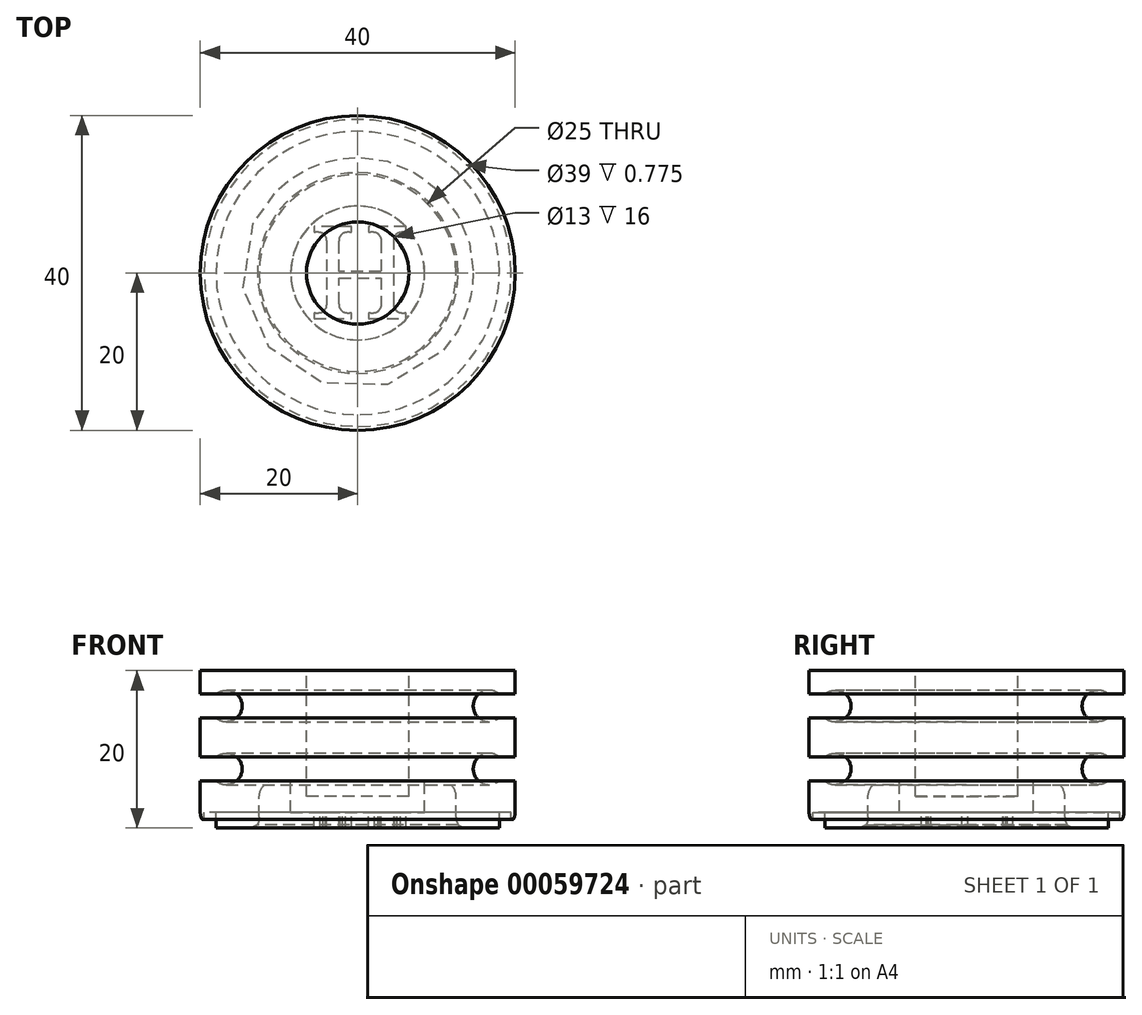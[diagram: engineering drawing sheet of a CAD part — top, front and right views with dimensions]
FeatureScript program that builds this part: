
annotation { "Feature Type Name" : "Feature", "Feature Type Description" : "" }
export const myFeature = defineFeature(function(context is Context, id is Id, definition is map)
    precondition{}
    {
        {
            var Q0;
            Q0=qCreatedBy(makeId("Top.planeOp"),FACE);
            var sketch = newSketch(context, id + "F0", { "sketchPlane" : qUnion([Q0])});
            skCircle(sketch, "E0", {"center": v(0, 0) * mm, "radius": 20 * mm});
            skSolve(sketch);
        }
        {
            var Q0;
            Q0=makeQuery(id+"F0.imprint","IMPRINT",FACE,{"disambiguationData":[TD([[makeQuery(id+"F0.imprint","IMPRINT",EDGE,{"derivedFrom":sQuery(id+"F0.wireOp",EDGE,"E0")}),1.0]])]});
            extrude(context, id + "F1", {"entities" : qUnion([Q0]), "depth" : 20 * mm});
        }
        {
            var Q0;
            Q0=qCreatedBy(makeId("Front.planeOp"),FACE);
            var sketch = newSketch(context, id + "F2", { "sketchPlane" : qUnion([Q0])});
            skLineSegment(sketch, "E1", {"start": v(-6.5, 20) * mm, "end": v(-20, 20) * mm});
            skLineSegment(sketch, "E2", {"start": v(-20, 20) * mm, "end": v(-20, 17) * mm});
            skLineSegment(sketch, "E3", {"start": v(-18, 0) * mm, "end": v(-13.97, 0) * mm});
            skLineSegment(sketch, "E4.bottom", {"start": v(-20, 17) * mm, "end": v(-18, 17) * mm});
            skLineSegment(sketch, "E4.top", {"start": v(-20, 14) * mm, "end": v(-18, 14) * mm});
            skLineSegment(sketch, "E5.bottom", {"start": v(-20, 9) * mm, "end": v(-18, 9) * mm});
            skLineSegment(sketch, "E5.top", {"start": v(-20, 6) * mm, "end": v(-18, 6) * mm});
            skArc(sketch, "E6", {"start": v(-18, 14) * mm, "mid": v(-14.68, 15.5) * mm, "end": v(-18, 17) * mm});
            skPoint(sketch, "E6.centerSnap0", {"position": v(-18, 15.5) * mm});
            skArc(sketch, "E7", {"start": v(-18, 6) * mm, "mid": v(-14.68, 7.5) * mm, "end": v(-18, 9) * mm});
            skPoint(sketch, "E7.centerSnap0", {"position": v(-18, 7.5) * mm});
            skLineSegment(sketch, "E8.trimOffspring", {"start": v(-20, 6) * mm, "end": v(-20, 2) * mm});
            skLineSegment(sketch, "E9.trimOffspring", {"start": v(-20, 14) * mm, "end": v(-20, 9) * mm});
            skLineSegment(sketch, "E10", {"start": v(0, 20) * mm, "end": v(0, 23.33) * mm});
            skLineSegment(sketch, "E11", {"start": v(0, 23.33) * mm, "end": v(-23.04, 23.33) * mm});
            skLineSegment(sketch, "E12", {"start": v(-23.04, 23.33) * mm, "end": v(-23.04, -1.84) * mm});
            skLineSegment(sketch, "E13", {"start": v(-23.04, -1.84) * mm, "end": v(0, -1.84) * mm});
            skLineSegment(sketch, "E14", {"start": v(0, -1.84) * mm, "end": v(0, 0) * mm});
            skLineSegment(sketch, "E15", {"start": v(0, 2) * mm, "end": v(0, 0) * mm});
            skLineSegment(sketch, "E16", {"start": v(-6.5, 20) * mm, "end": v(-6.5, 4) * mm});
            skLineSegment(sketch, "E17", {"start": v(-8.5, 6) * mm, "end": v(-10.5, 6) * mm});
            skLineSegment(sketch, "E18", {"start": v(-12.5, 4) * mm, "end": v(-12.5, 1.38) * mm});
            skLineSegment(sketch, "E19", {"start": v(-12.45, 0.7) * mm, "end": v(-12.98, 0.08) * mm});
            skPoint(sketch, "E20.visualSharp", {"position": v(-13.05, 0) * mm});
            skArc(sketch, "E20.filletArc", {"start": v(-13.97, 0) * mm, "mid": v(-13.13, 0.18) * mm, "end": v(-12.45, 0.7) * mm});
            skPoint(sketch, "E21.visualSharp", {"position": v(-12.5, 0.64) * mm});
            skArc(sketch, "E21.filletArc", {"start": v(-12.98, 0.08) * mm, "mid": v(-12.62, 0.69) * mm, "end": v(-12.5, 1.38) * mm});
            skPoint(sketch, "E22.visualSharp", {"position": v(-12.5, 4) * mm});
            skArc(sketch, "E22.filletArc", {"start": v(-10.5, 6) * mm, "mid": v(-11.91, 5.41) * mm, "end": v(-12.5, 4) * mm});
            skLineSegment(sketch, "E23", {"start": v(-8.5, 6) * mm, "end": v(-8.5, 2) * mm});
            skLineSegment(sketch, "E24", {"start": v(-8.5, 2) * mm, "end": v(0, 2) * mm});
            skLineSegment(sketch, "E25", {"start": v(0, 20) * mm, "end": v(0, 4) * mm});
            skLineSegment(sketch, "E26", {"start": v(-6.5, 4) * mm, "end": v(0, 4) * mm});
            skPoint(sketch, "E27.visualSharp", {"position": v(-20, 0) * mm});
            skArc(sketch, "E27.filletArc", {"start": v(-20, 2) * mm, "mid": v(-19.95, 1.57) * mm, "end": v(-19.81, 1.16) * mm});
            skLineSegment(sketch, "E28.top", {"start": v(-18, 2) * mm, "end": v(-19.5, 2) * mm});
            skLineSegment(sketch, "E28.left", {"start": v(-18, 0) * mm, "end": v(-18, 2) * mm});
            skLineSegment(sketch, "E28.right", {"start": v(-19.5, 1.22) * mm, "end": v(-19.5, 2) * mm});
            skPoint(sketch, "E29.visualSharp", {"position": v(-19.5, 0.68) * mm});
            skArc(sketch, "E29.filletArc", {"start": v(-19.81, 1.16) * mm, "mid": v(-19.63, 1.06) * mm, "end": v(-19.5, 1.22) * mm});
            skSolve(sketch);
        }
        {
            var Q0;
            Q0 = qSketchRegion(id + "F2", true);
            var Q1;
            Q1=makeQuery(id+"F1.opExtrude","CAP_EDGE",EDGE,{"disambiguationData":[OSD([sQuery(id+"F0.wireOp",EDGE,"E0")])],"isStart":false});
            revolve(context, id + "F3", {"operationType" : NewBodyOperationType.REMOVE, "entities" : qUnion([Q0]), "axis" : qUnion([Q1]), "revolveType" : RevolveType.FULL, "oppositeDirection" : true});
        }
        {
            var Q0;
            Q0=makeQuery(id+"F3.boolean.opBoolean","COPY",FACE,{"derivedFrom":makeQuery(id+"F3.opRevolve","SWEPT_FACE",FACE,{"disambiguationData":[OSD([sQuery(id+"F2.wireOp",EDGE,"E24")])]})});
            var sketch = newSketch(context, id + "F4", { "sketchPlane" : qUnion([Q0])});
            skText(sketch, "E30", { "text": "H", "fontName": "NotoSerif-Regular.ttf"});
            const initialGuessF4  = {"E30": [-0.00615, -0.00587, 1, 0, 0.01173]};
            skSetInitialGuess(sketch, initialGuessF4);
            skSolve(sketch);
        }
        {
            var Q0;
            Q0=makeQuery(id+"F4.imprint","IMPRINT",FACE,{"disambiguationData":[TD([[makeQuery(id+"F4.imprint","IMPRINT",EDGE,{"derivedFrom":sQuery(id+"F4.wireOp",EDGE,"E30.sketch_text.stroke-8")}),-1.0]])]});
            var Q1;
            Q1=makeQuery(id+"F4.imprint","IMPRINT",FACE,{"disambiguationData":[TD([[makeQuery(id+"F4.imprint","IMPRINT",EDGE,{"derivedFrom":sQuery(id+"F4.wireOp",EDGE,"E30.sketch_text.stroke-0")}),-1.0]])]});
            var Q2;
            Q2=makeQuery(id+"F4.imprint","IMPRINT",FACE,{"disambiguationData":[TD([[makeQuery(id+"F4.imprint","IMPRINT",EDGE,{"derivedFrom":sQuery(id+"F4.wireOp",EDGE,"E30.sketch_text.stroke-20")}),-1.0]])]});
            var Q3;
            Q3=makeQuery(id+"F4.imprint","IMPRINT",FACE,{"disambiguationData":[TD([[makeQuery(id+"F4.imprint","IMPRINT",EDGE,{"derivedFrom":sQuery(id+"F4.wireOp",EDGE,"E30.sketch_text.stroke-12")}),-1.0]])]});
            extrude(context, id + "F5", {"entities" : qUnion([Q0, Q1, Q2, Q3]), "operationType" : NewBodyOperationType.ADD, "depth" : 2 * mm});
        }
    });
